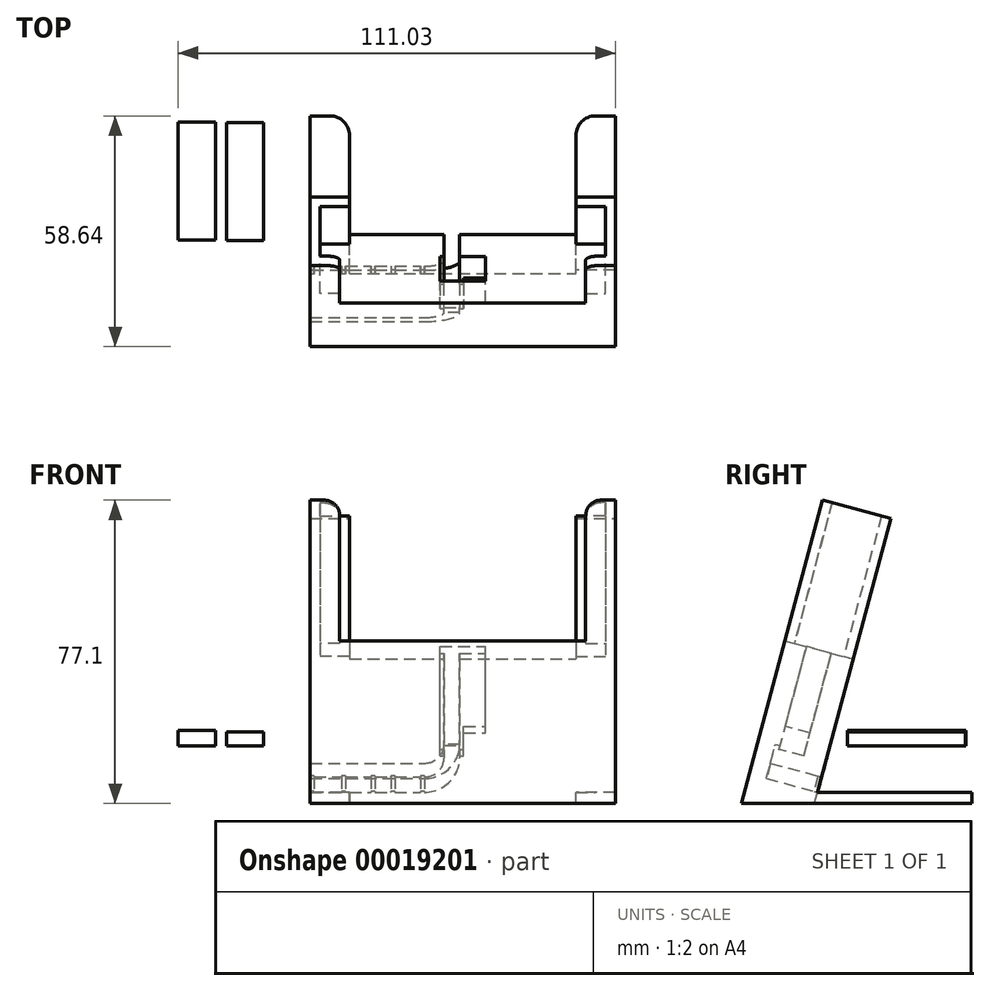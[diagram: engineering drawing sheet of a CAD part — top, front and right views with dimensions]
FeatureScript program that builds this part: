
annotation { "Feature Type Name" : "Feature", "Feature Type Description" : "" }
export const myFeature = defineFeature(function(context is Context, id is Id, definition is map)
    precondition{}
    {
        {
            var Q0;
            Q0=qCreatedBy(makeId("Top.planeOp"),FACE);
            var sketch = newSketch(context, id + "F0", { "sketchPlane" : qUnion([Q0])});
            skLineSegment(sketch, "E0.bottom", {"start": v(0, 0) * mm, "end": v(77.5, 0) * mm});
            skLineSegment(sketch, "E0.top", {"start": v(0, -18) * mm, "end": v(77.5, -18) * mm});
            skLineSegment(sketch, "E0.left", {"start": v(0, 0) * mm, "end": v(0, -18) * mm});
            skLineSegment(sketch, "E0.right", {"start": v(77.5, 0) * mm, "end": v(77.5, -18) * mm});
            skSolve(sketch);
        }
        {
            var Q0;
            Q0=qSketchRegion(id+"F0",true);
            var Q1;
            Q1=qSketchRegion(id+"F4",true);
            var Q2;
            Q2=qSketchRegion(id+"F2",true);
            extrude(context, id + "F1", {"entities" : qUnion([Q0, Q1, Q2]), "depth" : 3 * mm, "hasSecondDirection" : true, "secondDirectionOppositeDirection" : true, "secondDirectionDepth" : 35 * mm});
        }
        {
            var Q0;
            Q0=makeQuery(id+"F0.imprint","IMPRINT",FACE,{"disambiguationData":[TD([[makeQuery(id+"F0.imprint","IMPRINT",EDGE,{"derivedFrom":sQuery(id+"F0.wireOp",EDGE,"E0.bottom")}),-1.0]])]});
            var sketch = newSketch(context, id + "F2", { "sketchPlane" : qUnion([Q0])});
            skLineSegment(sketch, "E1.bottom", {"start": v(0, 0) * mm, "end": v(10, 0) * mm});
            skLineSegment(sketch, "E1.top", {"start": v(0, -2.5) * mm, "end": v(10, -2.5) * mm});
            skLineSegment(sketch, "E1.left", {"start": v(0, 0) * mm, "end": v(0, -2.5) * mm});
            skLineSegment(sketch, "E1.right", {"start": v(10, 0) * mm, "end": v(10, -2.5) * mm});
            skLineSegment(sketch, "E2.bottom", {"start": v(0, -2.5) * mm, "end": v(2.5, -2.5) * mm});
            skLineSegment(sketch, "E2.top", {"start": v(0, -18) * mm, "end": v(2.5, -18) * mm});
            skLineSegment(sketch, "E2.left", {"start": v(0, -2.5) * mm, "end": v(0, -18) * mm});
            skLineSegment(sketch, "E2.right", {"start": v(2.5, -2.5) * mm, "end": v(2.5, -18) * mm});
            skLineSegment(sketch, "E3.bottom", {"start": v(2.5, -15.5) * mm, "end": v(7.5, -15.5) * mm});
            skLineSegment(sketch, "E3.top", {"start": v(2.5, -18) * mm, "end": v(7.5, -18) * mm});
            skLineSegment(sketch, "E3.left", {"start": v(2.5, -15.5) * mm, "end": v(2.5, -18) * mm});
            skLineSegment(sketch, "E3.right", {"start": v(7.5, -15.5) * mm, "end": v(7.5, -18) * mm});
            skLineSegment(sketch, "E4", {"start": v(38.75, 38.6) * mm, "end": v(38.75, -47.5) * mm});
            skLineSegment(sketch, "E5.0.MirrorCS", {"start": v(77.5, -2.5) * mm, "end": v(75, -2.5) * mm});
            skLineSegment(sketch, "E5.1.MirrorCS", {"start": v(77.5, -18) * mm, "end": v(75, -18) * mm});
            skLineSegment(sketch, "E5.2.MirrorCS", {"start": v(67.5, 0) * mm, "end": v(67.5, -2.5) * mm});
            skLineSegment(sketch, "E5.3.MirrorCS", {"start": v(77.5, 0) * mm, "end": v(77.5, -2.5) * mm});
            skLineSegment(sketch, "E5.4.MirrorCS", {"start": v(75, -15.5) * mm, "end": v(75, -18) * mm});
            skLineSegment(sketch, "E5.5.MirrorCS", {"start": v(70, -15.5) * mm, "end": v(70, -18) * mm});
            skLineSegment(sketch, "E5.6.MirrorCS", {"start": v(77.5, -2.5) * mm, "end": v(77.5, -18) * mm});
            skLineSegment(sketch, "E5.7.MirrorCS", {"start": v(77.5, 0) * mm, "end": v(67.5, 0) * mm});
            skLineSegment(sketch, "E5.8.MirrorCS", {"start": v(77.5, -2.5) * mm, "end": v(67.5, -2.5) * mm});
            skLineSegment(sketch, "E5.9.MirrorCS", {"start": v(75, -2.5) * mm, "end": v(75, -18) * mm});
            skLineSegment(sketch, "E5.10.MirrorCS", {"start": v(75, -18) * mm, "end": v(70, -18) * mm});
            skLineSegment(sketch, "E5.11.MirrorCS", {"start": v(75, -15.5) * mm, "end": v(70, -15.5) * mm});
            skSolve(sketch);
        }
        {
            var Q0;
            Q0=qSketchRegion(id+"F2",true);
            var Q1;
            Q1=qSketchRegion(id+"F4",true);
            extrude(context, id + "F3", {"entities" : qUnion([Q0, Q1]), "operationType" : NewBodyOperationType.ADD, "depth" : 40 * mm});
        }
        {
            var Q0;
            Q0=makeQuery(id+"F1.opExtrude","CAP_FACE",FACE,{"disambiguationData":[OSD([sQuery(id+"F0.wireOp",EDGE,"E0.bottom"),sQuery(id+"F0.wireOp",EDGE,"E0.top"),sQuery(id+"F0.wireOp",EDGE,"E0.left"),sQuery(id+"F0.wireOp",EDGE,"E0.right")])],"isStart":false});
            var sketch = newSketch(context, id + "F4", { "sketchPlane" : qUnion([Q0])});
            skLineSegment(sketch, "E6.bottom", {"start": v(33, -5.75) * mm, "end": v(44.5, -5.75) * mm});
            skLineSegment(sketch, "E6.top", {"start": v(33, -12.25) * mm, "end": v(44.5, -12.25) * mm});
            skLineSegment(sketch, "E6.left", {"start": v(33, -5.75) * mm, "end": v(33, -12.25) * mm});
            skLineSegment(sketch, "E6.right", {"start": v(44.5, -5.75) * mm, "end": v(44.5, -12.25) * mm});
            skSolve(sketch);
        }
        {
            var Q0;
            Q0=qSketchRegion(id+"F4",true);
            extrude(context, id + "F5", {"entities" : qUnion([Q0]), "operationType" : NewBodyOperationType.REMOVE, "oppositeDirection" : true, "depth" : 21 * mm});
        }
        {
            var Q0;
            Q0=makeQuery(id+"F5.boolean.opBoolean","COPY",FACE,{"derivedFrom":makeQuery(id+"F5.opExtrude","CAP_FACE",FACE,{"disambiguationData":[OSD([sQuery(id+"F4.wireOp",EDGE,"E6.bottom"),sQuery(id+"F4.wireOp",EDGE,"E6.top"),sQuery(id+"F4.wireOp",EDGE,"E6.left"),sQuery(id+"F4.wireOp",EDGE,"E6.right")])],"isStart":false})});
            var sketch = newSketch(context, id + "F6", { "sketchPlane" : qUnion([Q0])});
            skLineSegment(sketch, "E7.bottom", {"start": v(33, -5.75) * mm, "end": v(39, -5.75) * mm});
            skLineSegment(sketch, "E7.top", {"start": v(33, -12.25) * mm, "end": v(39, -12.25) * mm});
            skLineSegment(sketch, "E7.left", {"start": v(33, -5.75) * mm, "end": v(33, -12.25) * mm});
            skLineSegment(sketch, "E7.right", {"start": v(39, -5.75) * mm, "end": v(39, -12.25) * mm});
            skSolve(sketch);
        }
        {
            var Q0;
            Q0=qSketchRegion(id+"F6",true);
            var Q1;
            Q1 = qSketchRegion(id + "F4", true);
            extrude(context, id + "F7", {"entities" : qUnion([Q0, Q1]), "operationType" : NewBodyOperationType.REMOVE, "oppositeDirection" : true, "depth" : 6 * mm});
        }
        {
            var Q0;
            Q0=makeQuery(id+"F3.boolean.opBoolean","MERGE",FACE,{"derivedFrom":[makeQuery(id+"F1.opExtrude","SWEPT_FACE",FACE,{"disambiguationData":[OSD([sQuery(id+"F0.wireOp",EDGE,"E0.bottom")])]}),makeQuery(id+"F3.opExtrude","SWEPT_FACE",FACE,{"disambiguationData":[OSD([sQuery(id+"F2.wireOp",EDGE,"E1.bottom")])]}),makeQuery(id+"F3.opExtrude","SWEPT_FACE",FACE,{"disambiguationData":[OSD([sQuery(id+"F2.wireOp",EDGE,"E5.7.MirrorCS")])]})]});
            var sketch = newSketch(context, id + "F8", { "sketchPlane" : qUnion([Q0])});
            skLineSegment(sketch, "E8.bottom", {"start": v(0, -32) * mm, "end": v(-29, -32) * mm});
            skLineSegment(sketch, "E8.top", {"start": v(0, -28) * mm, "end": v(-29, -28) * mm});
            skLineSegment(sketch, "E8.left", {"start": v(0, -32) * mm, "end": v(0, -28) * mm});
            skLineSegment(sketch, "E8.right", {"start": v(-29, -32) * mm, "end": v(-29, -28) * mm});
            skSolve(sketch);
        }
        {
            var Q0;
            Q0=qSketchRegion(id+"F8",true);
            extrude(context, id + "F9", {"entities" : qUnion([Q0]), "operationType" : NewBodyOperationType.REMOVE, "oppositeDirection" : true, "depth" : 13.5 * mm});
        }
        {
            var Q0;
            Q0=makeQuery(id+"F3.boolean.opBoolean","MERGE",FACE,{"derivedFrom":[makeQuery(id+"F1.opExtrude","SWEPT_FACE",FACE,{"disambiguationData":[OSD([sQuery(id+"F0.wireOp",EDGE,"E0.top")])]}),makeQuery(id+"F3.opExtrude","SWEPT_FACE",FACE,{"disambiguationData":[OSD([sQuery(id+"F2.wireOp",EDGE,"E2.top"),sQuery(id+"F2.wireOp",EDGE,"E3.top")])]}),makeQuery(id+"F3.opExtrude","SWEPT_FACE",FACE,{"disambiguationData":[OSD([sQuery(id+"F2.wireOp",EDGE,"E5.1.MirrorCS"),sQuery(id+"F2.wireOp",EDGE,"E5.10.MirrorCS")])]})]});
            cPlane(context, id + "F10", {"entities" : qUnion([Q0]), "cplaneType" : CPlaneType.OFFSET, "offset" : 10 * mm, "oppositeDirection" : true, "width" : 150 * mm, "height" : 150 * mm});
        }
        {
            var Q0;
            Q0=qCreatedBy(makeId("Right.planeOp"),FACE);
            cPlane(context, id + "F11", {"entities" : qUnion([Q0]), "cplaneType" : CPlaneType.OFFSET, "offset" : 38.75 * mm, "width" : 150 * mm, "height" : 150 * mm});
        }
        {
            var Q0;
            Q0=makeQuery(id+"F1.opExtrude","CAP_FACE",FACE,{"disambiguationData":[OSD([sQuery(id+"F0.wireOp",EDGE,"E0.bottom"),sQuery(id+"F0.wireOp",EDGE,"E0.top"),sQuery(id+"F0.wireOp",EDGE,"E0.left"),sQuery(id+"F0.wireOp",EDGE,"E0.right")])],"isStart":false});
            cPlane(context, id + "F12", {"entities" : qUnion([Q0]), "cplaneType" : CPlaneType.OFFSET, "offset" : 34 * mm, "oppositeDirection" : true, "width" : 150 * mm, "height" : 150 * mm});
        }
        {
            var Q0;
            Q0=qCreatedBy(id+"F12.planeOp",FACE);
            cPlane(context, id + "F13", {"entities" : qUnion([Q0]), "cplaneType" : CPlaneType.OFFSET, "offset" : 6 * mm, "width" : 150 * mm, "height" : 150 * mm});
        }
        {
            var Q0;
            Q0=qCreatedBy(id+"F10.planeOp",FACE);
            var sketch = newSketch(context, id + "F14", { "sketchPlane" : qUnion([Q0])});
            skArc(sketch, "E9", {"start": v(29, -31) * mm, "mid": v(34.66, -28.66) * mm, "end": v(37, -23) * mm});
            skSolve(sketch);
        }
        {
            var Q0;
            Q0=makeQuery(id+"F9.boolean.opBoolean","COPY",FACE,{"derivedFrom":makeQuery(id+"F9.opExtrude","SWEPT_FACE",FACE,{"disambiguationData":[OSD([sQuery(id+"F8.wireOp",EDGE,"E8.right")])]})});
            var Q1;
            Q1=sQuery(id+"F14.wireOp",EDGE,"E9");
            sweep(context, id + "F15", {"operationType" : NewBodyOperationType.REMOVE, "profiles" : qUnion([Q0]), "path" : qUnion([Q1])});
        }
        {
            var Q0;
            Q0=makeQuery(id+"F3.boolean.opBoolean","MERGE",FACE,{"derivedFrom":[makeQuery(id+"F1.opExtrude","SWEPT_FACE",FACE,{"disambiguationData":[OSD([sQuery(id+"F0.wireOp",EDGE,"E0.bottom")])]}),makeQuery(id+"F3.opExtrude","SWEPT_FACE",FACE,{"disambiguationData":[OSD([sQuery(id+"F2.wireOp",EDGE,"E1.bottom")])]}),makeQuery(id+"F3.opExtrude","SWEPT_FACE",FACE,{"disambiguationData":[OSD([sQuery(id+"F2.wireOp",EDGE,"E5.7.MirrorCS")])]})]});
            var sketch = newSketch(context, id + "F16", { "sketchPlane" : qUnion([Q0])});
            skLineSegment(sketch, "E10.bottom", {"start": v(-38, 3) * mm, "end": v(-34, 3) * mm});
            skLineSegment(sketch, "E10.top", {"start": v(-38, -23) * mm, "end": v(-34, -23) * mm});
            skLineSegment(sketch, "E10.left", {"start": v(-38, 3) * mm, "end": v(-38, -23) * mm});
            skLineSegment(sketch, "E10.right", {"start": v(-34, 3) * mm, "end": v(-34, -23) * mm});
            skSolve(sketch);
        }
        {
            var Q0;
            Q0=qSketchRegion(id+"F16",true);
            extrude(context, id + "F17", {"entities" : qUnion([Q0]), "operationType" : NewBodyOperationType.REMOVE, "oppositeDirection" : true, "depth" : 7 * mm});
        }
        {
            var Q0;
            Q0=makeQuery(id+"F1.opExtrude","SWEPT_BODY",BODY,{"disambiguationData":[OSD([sQuery(id+"F0.wireOp",EDGE,"E0.bottom"),sQuery(id+"F0.wireOp",EDGE,"E0.top"),sQuery(id+"F0.wireOp",EDGE,"E0.left"),sQuery(id+"F0.wireOp",EDGE,"E0.right")])]});
            var Q1;
            Q1=makeQuery(id+"F1.opExtrude","CAP_EDGE",EDGE,{"disambiguationData":[OSD([sQuery(id+"F0.wireOp",EDGE,"E0.top")])],"isStart":true});
            transform(context, id + "F18", {"entities" : qUnion([Q0]), "transformType" : TransformType.ROTATION, "transformAxis" : qUnion([Q1]), "angle" : 15 * degree, "oppositeDirection" : true, "makeCopy" : false});
        }
        {
            var Q0;
            Q0=makeQuery(id+"F3.boolean.opBoolean","MERGE",FACE,{"derivedFrom":[makeQuery(id+"F1.opExtrude","SWEPT_FACE",FACE,{"disambiguationData":[OSD([sQuery(id+"F0.wireOp",EDGE,"E0.right")])]}),makeQuery(id+"F3.opExtrude","SWEPT_FACE",FACE,{"disambiguationData":[OSD([sQuery(id+"F2.wireOp",EDGE,"E5.3.MirrorCS"),sQuery(id+"F2.wireOp",EDGE,"E5.6.MirrorCS")])]})]});
            var sketch = newSketch(context, id + "F19", { "sketchPlane" : qUnion([Q0])});
            skLineSegment(sketch, "E11", {"start": v(-18, -35) * mm, "end": v(-19.25, -39.66) * mm});
            skLineSegment(sketch, "E12", {"start": v(-19.25, -39.66) * mm, "end": v(-0.61, -39.66) * mm});
            skLineSegment(sketch, "E13", {"start": v(-0.61, -39.66) * mm, "end": v(-18, -35) * mm});
            skSolve(sketch);
        }
        {
            var Q0;
            Q0=makeQuery(id+"F19.imprint","IMPRINT",FACE,{"disambiguationData":[TD([[makeQuery(id+"F19.imprint","IMPRINT",EDGE,{"derivedFrom":sQuery(id+"F19.wireOp",EDGE,"E11")}),1.0]])]});
            extrude(context, id + "F20", {"entities" : qUnion([Q0]), "operationType" : NewBodyOperationType.ADD, "oppositeDirection" : true, "depth" : 77.5 * mm});
        }
        {
            var Q0;
            Q0=makeQuery(id+"F20.opExtrude","SWEPT_FACE",FACE,{"disambiguationData":[OSD([sQuery(id+"F19.wireOp",EDGE,"E12")])]});
            var sketch = newSketch(context, id + "F21", { "sketchPlane" : qUnion([Q0])});
            skLineSegment(sketch, "E14.bottom", {"start": v(0, 0.61) * mm, "end": v(10, 0.61) * mm});
            skLineSegment(sketch, "E14.top", {"start": v(0, -39.39) * mm, "end": v(10, -39.39) * mm});
            skLineSegment(sketch, "E14.left", {"start": v(0, 0.61) * mm, "end": v(0, -39.39) * mm});
            skLineSegment(sketch, "E14.right", {"start": v(10, 0.61) * mm, "end": v(10, -39.39) * mm});
            skLineSegment(sketch, "E15.MirrorCS", {"start": v(77.5, 0.61) * mm, "end": v(77.5, -39.39) * mm});
            skLineSegment(sketch, "E16.MirrorCS", {"start": v(67.5, 0.61) * mm, "end": v(67.5, -39.39) * mm});
            skLineSegment(sketch, "E17.MirrorCS", {"start": v(77.5, -39.39) * mm, "end": v(67.5, -39.39) * mm});
            skLineSegment(sketch, "E18.MirrorCS", {"start": v(77.5, 0.61) * mm, "end": v(67.5, 0.61) * mm});
            skSolve(sketch);
        }
        {
            var Q0;
            Q0=qSketchRegion(id+"F21",true);
            extrude(context, id + "F22", {"entities" : qUnion([Q0]), "operationType" : NewBodyOperationType.ADD, "oppositeDirection" : true, "depth" : 2.9 * mm});
        }
        {
            var Q0;
            Q0=makeQuery(id+"F3.opExtrude","CAP_EDGE",EDGE,{"disambiguationData":[OSD([sQuery(id+"F2.wireOp",EDGE,"E3.right")])],"isStart":false});
            fillet(context, id + "F23", {"entities" : qUnion([Q0]), "radius" : 4 * mm, "tangentPropagation" : true, "allowEdgeOverflow" : false});
        }
        {
            var Q0;
            Q0=makeQuery(id+"F3.opExtrude","CAP_EDGE",EDGE,{"disambiguationData":[OSD([sQuery(id+"F2.wireOp",EDGE,"E5.5.MirrorCS")])],"isStart":false});
            fillet(context, id + "F24", {"entities" : qUnion([Q0]), "radius" : 4 * mm, "tangentPropagation" : true, "allowEdgeOverflow" : false});
        }
        {
            var Q0;
            Q0=makeQuery(id+"F22.opExtrude","SWEPT_EDGE",EDGE,{"disambiguationData":[OSD([sQuery(id+"F21.wireOp",EDGE,"E14.top"),sQuery(id+"F21.wireOp",EDGE,"E14.right")])]});
            fillet(context, id + "F25", {"entities" : qUnion([Q0]), "radius" : 5 * mm, "tangentPropagation" : true, "allowEdgeOverflow" : false});
        }
        {
            var Q0;
            Q0=makeQuery(id+"F22.opExtrude","SWEPT_EDGE",EDGE,{"disambiguationData":[OSD([sQuery(id+"F21.wireOp",EDGE,"E16.MirrorCS"),sQuery(id+"F21.wireOp",EDGE,"E17.MirrorCS")])]});
            fillet(context, id + "F26", {"entities" : qUnion([Q0]), "radius" : 5 * mm, "tangentPropagation" : true, "allowEdgeOverflow" : false});
        }
        {
            var Q0;
            Q0=makeQuery(id+"F9.boolean.opBoolean","COPY",FACE,{"derivedFrom":makeQuery(id+"F9.opExtrude","SWEPT_FACE",FACE,{"disambiguationData":[OSD([sQuery(id+"F8.wireOp",EDGE,"E8.bottom")])]})});
            var sketch = newSketch(context, id + "F27", { "sketchPlane" : qUnion([Q0])});
            skLineSegment(sketch, "E19.bottom", {"start": v(1, 8.66) * mm, "end": v(0, 8.66) * mm});
            skLineSegment(sketch, "E19.top", {"start": v(1, 9.66) * mm, "end": v(0, 9.66) * mm});
            skLineSegment(sketch, "E19.left", {"start": v(1, 8.66) * mm, "end": v(1, 9.66) * mm});
            skLineSegment(sketch, "E19.right", {"start": v(0, 8.66) * mm, "end": v(0, 9.66) * mm});
            skLineSegment(sketch, "E20.bottom", {"start": v(29, 8.67) * mm, "end": v(28, 8.67) * mm});
            skLineSegment(sketch, "E20.top", {"start": v(29, 9.67) * mm, "end": v(28, 9.67) * mm});
            skLineSegment(sketch, "E20.left", {"start": v(29, 8.67) * mm, "end": v(29, 9.67) * mm});
            skLineSegment(sketch, "E20.right", {"start": v(28, 8.67) * mm, "end": v(28, 9.67) * mm});
            skLineSegment(sketch, "E21.bottom", {"start": v(16.5, 8.67) * mm, "end": v(15.5, 8.67) * mm});
            skLineSegment(sketch, "E21.top", {"start": v(16.5, 9.67) * mm, "end": v(15.5, 9.67) * mm});
            skLineSegment(sketch, "E21.left", {"start": v(16.5, 8.67) * mm, "end": v(16.5, 9.67) * mm});
            skLineSegment(sketch, "E21.right", {"start": v(15.5, 8.67) * mm, "end": v(15.5, 9.67) * mm});
            skLineSegment(sketch, "E22.bottom", {"start": v(21.5, 9.67) * mm, "end": v(20.5, 9.67) * mm});
            skLineSegment(sketch, "E22.top", {"start": v(21.5, 8.67) * mm, "end": v(20.5, 8.67) * mm});
            skLineSegment(sketch, "E22.left", {"start": v(21.5, 9.67) * mm, "end": v(21.5, 8.67) * mm});
            skLineSegment(sketch, "E22.right", {"start": v(20.5, 9.67) * mm, "end": v(20.5, 8.67) * mm});
            skLineSegment(sketch, "E23.bottom", {"start": v(9, 8.66) * mm, "end": v(8, 8.66) * mm});
            skLineSegment(sketch, "E23.top", {"start": v(9, 9.66) * mm, "end": v(8, 9.66) * mm});
            skLineSegment(sketch, "E23.left", {"start": v(9, 8.66) * mm, "end": v(9, 9.66) * mm});
            skLineSegment(sketch, "E23.right", {"start": v(8, 8.66) * mm, "end": v(8, 9.66) * mm});
            skSolve(sketch);
        }
        {
            var Q0;
            Q0=qSketchRegion(id+"F27",true);
            extrude(context, id + "F28", {"entities" : qUnion([Q0]), "operationType" : NewBodyOperationType.ADD, "depth" : 4 * mm});
        }
        {
            var Q0;
            Q0=qCreatedBy(id+"F13.planeOp",FACE);
            var sketch = newSketch(context, id + "F29", { "sketchPlane" : qUnion([Q0])});
            skLineSegment(sketch, "E24.bottom", {"start": v(-21.3, 37.74) * mm, "end": v(-11.8, 37.74) * mm});
            skLineSegment(sketch, "E24.top", {"start": v(-21.3, 7.74) * mm, "end": v(-11.8, 7.74) * mm});
            skLineSegment(sketch, "E24.left", {"start": v(-21.3, 37.74) * mm, "end": v(-21.3, 7.74) * mm});
            skLineSegment(sketch, "E24.right", {"start": v(-11.8, 37.74) * mm, "end": v(-11.8, 7.74) * mm});
            skSolve(sketch);
        }
        {
            var Q0;
            Q0=qSketchRegion(id+"F29",true);
            extrude(context, id + "F30", {"entities" : qUnion([Q0]), "depth" : 3.5 * mm});
        }
        {
            var Q0;
            Q0=qCreatedBy(id+"F13.planeOp",FACE);
            var sketch = newSketch(context, id + "F31", { "sketchPlane" : qUnion([Q0])});
            skLineSegment(sketch, "E25.bottom", {"start": v(-24.03, 7.78) * mm, "end": v(-33.53, 7.78) * mm});
            skLineSegment(sketch, "E25.top", {"start": v(-24.03, 37.78) * mm, "end": v(-33.53, 37.78) * mm});
            skLineSegment(sketch, "E25.left", {"start": v(-24.03, 7.78) * mm, "end": v(-24.03, 37.78) * mm});
            skLineSegment(sketch, "E25.right", {"start": v(-33.53, 7.78) * mm, "end": v(-33.53, 37.78) * mm});
            skSolve(sketch);
        }
        {
            var Q0;
            Q0=qSketchRegion(id+"F31",true);
            extrude(context, id + "F32", {"entities" : qUnion([Q0]), "depth" : 4 * mm});
        }
    });
